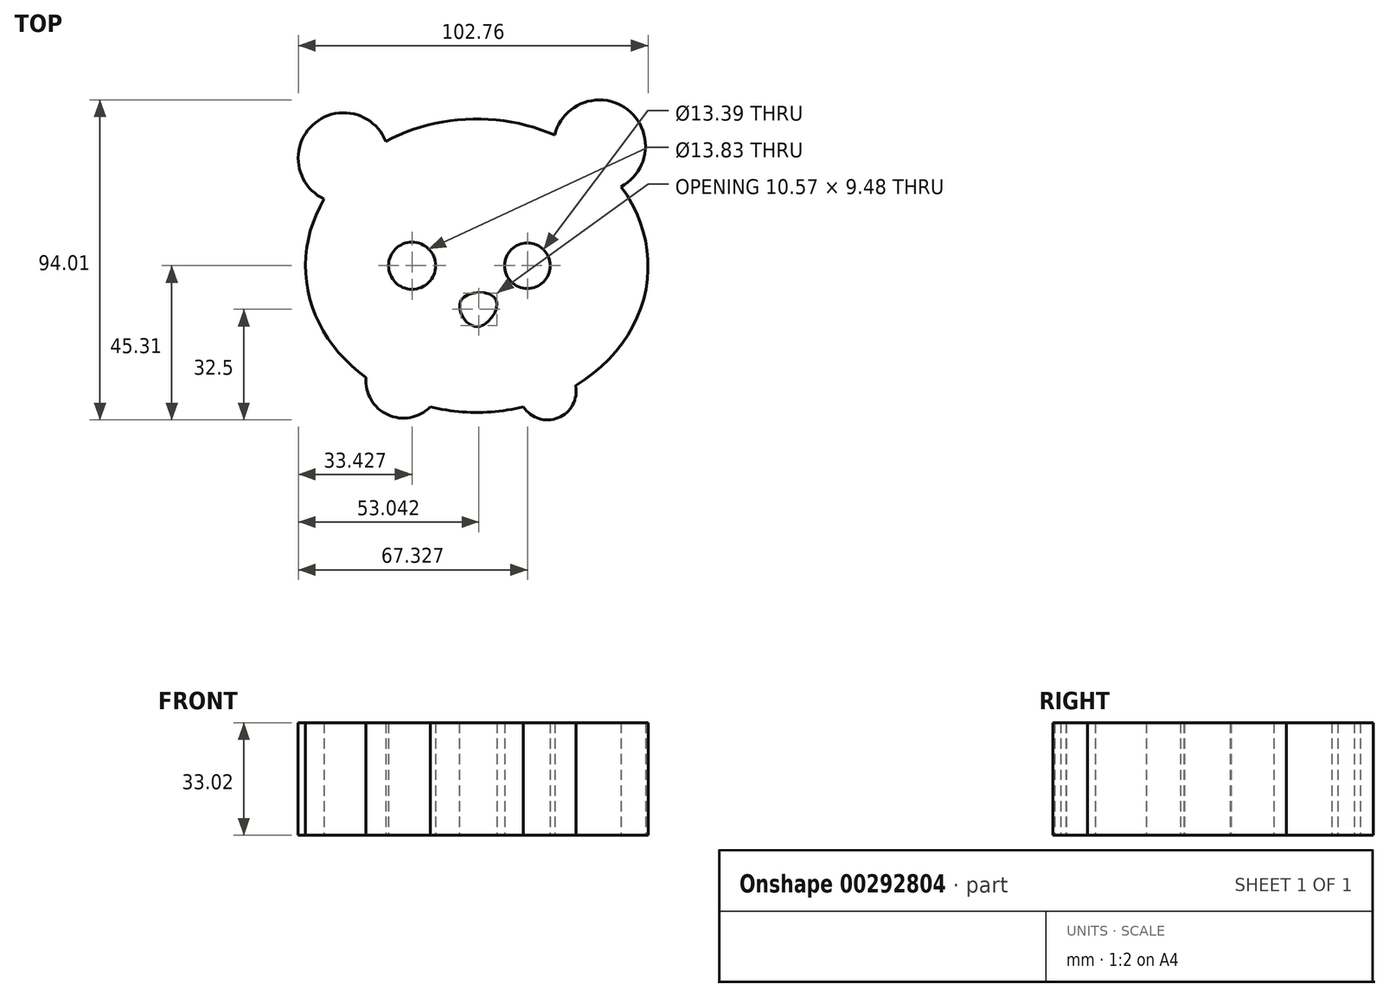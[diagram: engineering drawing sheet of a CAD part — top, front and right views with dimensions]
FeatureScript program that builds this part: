
annotation { "Feature Type Name" : "Feature", "Feature Type Description" : "" }
export const myFeature = defineFeature(function(context is Context, id is Id, definition is map)
    precondition{}
    {
        {
            var Q0;
            Q0=qCreatedBy(makeId("Top.planeOp"),FACE);
            var sketch = newSketch(context, id + "F0", { "sketchPlane" : qUnion([Q0])});
            skEllipticalArc(sketch, "E0", {});
            skArc(sketch, "E1", {"start": v(42.38, 23.23) * mm, "mid": v(44.32, 45.86) * mm, "end": v(22.88, 38.4) * mm});
            skArc(sketch, "E2", {"start": v(-26.73, 36.52) * mm, "mid": v(-48.22, 41.34) * mm, "end": v(-44.83, 19.57) * mm});
            skCircle(sketch, "E3", {"center": v(14.89, 0) * mm, "radius": 6.7 * mm});
            skCircle(sketch, "E4", {"center": v(-19.01, 0) * mm, "radius": 6.92 * mm});
            skFitSpline(sketch, "E5", {"points": [v(-4.61, -10.11) * mm, v(5.59, -9.81) * mm, v(0, -17.91) * mm, v(-4.61, -10.11) * mm]});
            skArc(sketch, "E6", {"start": v(-32.55, -32.87) * mm, "mid": v(-26.14, -43.79) * mm, "end": v(-13.69, -41.48) * mm});
            skArc(sketch, "E7", {"start": v(13.7, -41.48) * mm, "mid": v(23.95, -44.68) * mm, "end": v(29.03, -35.2) * mm});
            skEllipticalArc(sketch, "E8.trimOffspring", {});
            skEllipticalArc(sketch, "E9.trimOffspring", {});
            skEllipticalArc(sketch, "E10.trimOffspring", {});
            const initialGuessF0  = {"E0": [0, 0, 1, 0, 0.05031828029015022, 0.043104516280707834, 5.327315082949227, 0.5692046673743629], "E8.trimOffspring": [0, 0, 1, 0, 0.05031828029015022, 0.043104516280707834, 4.436948517300046, 4.987972011437749], "E9.trimOffspring": [0, 0, 1, 0, 0.05031828029015022, 0.043104516280707834, 1.0988176954039446, 2.1307691563612727], "E10.trimOffspring": [0, 0, 1, 0, 0.05031828029015022, 0.043104516280707834, 2.670304247665652, 4.008898416059354]};
            skSetInitialGuess(sketch, initialGuessF0);
            skSolve(sketch);
        }
        {
            var Q0;
            Q0=makeQuery(id+"F0.imprint","IMPRINT",FACE,{"disambiguationData":[TD([[makeQuery(id+"F0.imprint","IMPRINT",EDGE,{"derivedFrom":sQuery(id+"F0.wireOp",EDGE,"E0")}),1.0]])]});
            extrude(context, id + "F1", {"entities" : qUnion([Q0]), "depth" : 33.02 * mm});
        }
    });
